# Revit family: Kohler Ladena 2215IN-0 Family
name_source: partatom
category: Plumbing Fixtures
revit_build: Autodesk Revit 2018 (Build: 20180329_1100(x64)
units: mm (PartAtom-declared; Revit-internal decimal feet)

## family parameters
Always vertical = Yes
Cut with Voids When Loaded = Yes
OmniClass Number = 23.45.05.14.14
OmniClass Title = Sinks/Lavatories
Part Type = Normal
Room Calculation Point = No
Round Connector Dimension = Use Radius
Shared = No
Work Plane-Based = Yes

## types (10) — shared parameters
Default Elevation = 1219.2 mm  [stored 4 ft]
Drain Flow = 0 GPM
Drain Radius = 22.225 mm  [stored 0.0729167 ft]

## per-type parameters (varying)
| type | Description | Manufacturer | Model | Product Material | Type Image | URL |
| White | See Part Description | Kohler Company | See Part Number | Vitreous China - Kohler - White | <None> | http://www.us.kohler.com |
| Biscuit | See Part Description | Kohler Company | See Part Number | Vitreous China - Kohler - Biscuit | <None> | http://www.us.kohler.com |
| Almond | See Part Description | Kohler Company | See Part Number | Vitreous China - Kohler - Almond | <None> | http://www.us.kohler.com |
| Dune | See Part Description | Kohler Company | See Part Number | Vitreous China - Kohler - Dune | <None> | http://www.us.kohler.com |
| Ice Grey | See Part Description | Kohler Company | See Part Number | Vitreous China - Kohler - Ice Grey | <None> | http://www.us.kohler.com |
| Sandbar | See Part Description | Kohler Company | See Part Number | Vitreous China - Kohler - Sandbar | <None> | http://www.us.kohler.com |
| Mexican Sand | See Part Description | Kohler Company | See Part Number | Vitreous China - Kohler - Mexican Sand | <None> | http://www.us.kohler.com |
| Cashmere | See Part Description | Kohler Company | See Part Number | Vitreous China - Kohler - Cashmere | <None> | http://www.us.kohler.com |
| Thunder Grey | See Part Description | Kohler Company | See Part Number | Vitreous China - Kohler - Thunder Grey | <None> | http://www.us.kohler.com |
| Kohler 2215IN-0 | Undercounter basin | kohler | Ladena 2215IN-0 | Vitreous China - Kohler - Black | 2215IN-0.tif | www.us.kohler.com |

note: [stored X ft] marks values corroborated as IEEE doubles in the binary element streams (Revit-internal decimal feet)

## geometry (parser evidence)
native form markers: Blend x40, Sweep x1
no freeform markers — native parametric forms only
